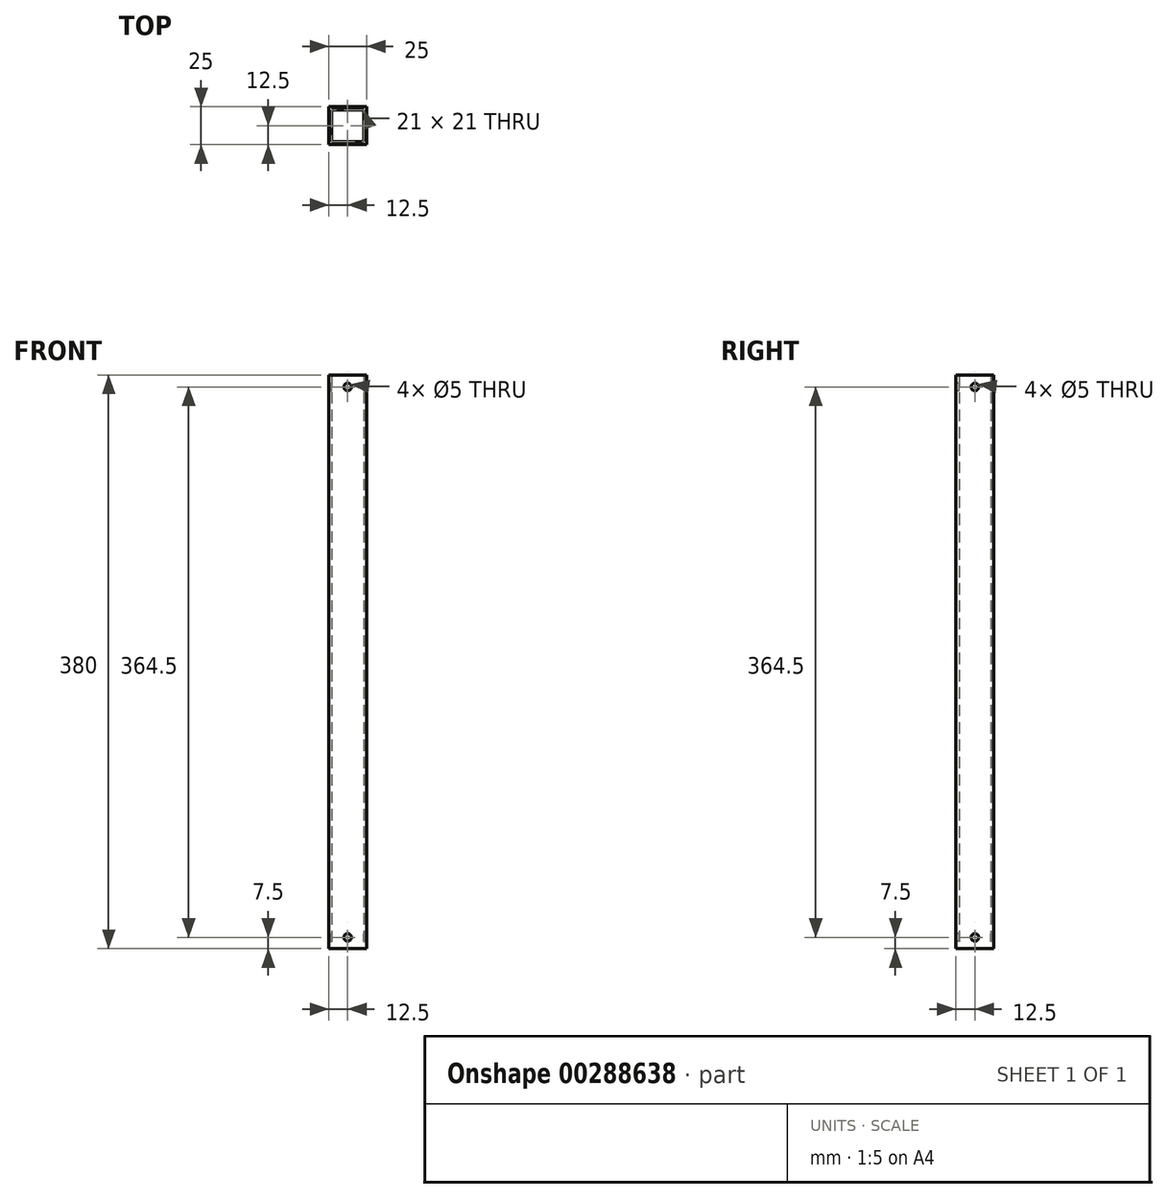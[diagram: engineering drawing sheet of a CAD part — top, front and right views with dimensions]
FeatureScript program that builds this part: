
annotation { "Feature Type Name" : "Feature", "Feature Type Description" : "" }
export const myFeature = defineFeature(function(context is Context, id is Id, definition is map)
    precondition{}
    {
        {
            var Q0;
            Q0=qCreatedBy(makeId("Top.planeOp"),FACE);
            var sketch = newSketch(context, id + "F0", { "sketchPlane" : qUnion([Q0])});
            skLineSegment(sketch, "E0.bottom", {"start": v(10.5, 10.5) * mm, "end": v(-10.5, 10.5) * mm});
            skLineSegment(sketch, "E0.top", {"start": v(10.5, -10.5) * mm, "end": v(-10.5, -10.5) * mm});
            skLineSegment(sketch, "E0.left", {"start": v(10.5, 10.5) * mm, "end": v(10.5, -10.5) * mm});
            skLineSegment(sketch, "E0.right", {"start": v(-10.5, 10.5) * mm, "end": v(-10.5, -10.5) * mm});
            skPoint(sketch, "E0.middle", {"position": v(0, 0) * mm});
            skLineSegment(sketch, "E1.bottom", {"start": v(12.5, 12.5) * mm, "end": v(-12.5, 12.5) * mm});
            skLineSegment(sketch, "E1.top", {"start": v(12.5, -12.5) * mm, "end": v(-12.5, -12.5) * mm});
            skLineSegment(sketch, "E1.left", {"start": v(12.5, 12.5) * mm, "end": v(12.5, -12.5) * mm});
            skLineSegment(sketch, "E1.right", {"start": v(-12.5, 12.5) * mm, "end": v(-12.5, -12.5) * mm});
            skSolve(sketch);
        }
        {
            var Q0;
            Q0=makeQuery(id+"F0.imprint","IMPRINT",FACE,{"disambiguationData":[TD([[makeQuery(id+"F0.imprint","IMPRINT",EDGE,{"derivedFrom":sQuery(id+"F0.wireOp",EDGE,"E0.bottom")}),-1.0]])]});
            extrude(context, id + "F1", {"entities" : qUnion([Q0]), "depth" : 380 * mm});
        }
        {
            var Q0;
            Q0=makeQuery(id+"F1.opExtrude","SWEPT_FACE",FACE,{"disambiguationData":[OSD([sQuery(id+"F0.wireOp",EDGE,"E1.top")])]});
            var sketch = newSketch(context, id + "F2", { "sketchPlane" : qUnion([Q0])});
            skCircle(sketch, "E2", {"center": v(0, 372) * mm, "radius": 2.5 * mm});
            skPoint(sketch, "E2.centerSnap0", {"position": v(0, 380) * mm});
            skCircle(sketch, "E3", {"center": v(0, 7.5) * mm, "radius": 2.5 * mm});
            skSolve(sketch);
        }
        {
            var Q0;
            Q0=makeQuery(id+"F2.imprint","IMPRINT",FACE,{"disambiguationData":[TD([[makeQuery(id+"F2.imprint","IMPRINT",EDGE,{"derivedFrom":sQuery(id+"F2.wireOp",EDGE,"E2")}),1.0]])]});
            var Q1;
            Q1=makeQuery(id+"F2.imprint","IMPRINT",FACE,{"disambiguationData":[TD([[makeQuery(id+"F2.imprint","IMPRINT",EDGE,{"derivedFrom":sQuery(id+"F2.wireOp",EDGE,"E3")}),1.0]])]});
            var Q2;
            Q2=sQuery(id+"F2.wireOp",EDGE,"E2");
            extrude(context, id + "F3", {"entities" : qUnion([Q0, Q1]), "operationType" : NewBodyOperationType.REMOVE, "surfaceEntities" : qUnion([Q2]), "oppositeDirection" : true, "depth" : 25 * mm, "offsetDistance" : 25 * mm});
        }
        {
            var Q0;
            Q0=makeQuery(id+"F1.opExtrude","SWEPT_FACE",FACE,{"disambiguationData":[OSD([sQuery(id+"F0.wireOp",EDGE,"E1.left")])]});
            var sketch = newSketch(context, id + "F4", { "sketchPlane" : qUnion([Q0])});
            skCircle(sketch, "E4", {"center": v(0, 7.5) * mm, "radius": 2.5 * mm});
            skPoint(sketch, "E4.centerSnap0", {"position": v(0, 0) * mm});
            skCircle(sketch, "E5", {"center": v(0, 372) * mm, "radius": 2.5 * mm});
            skPoint(sketch, "E5.centerSnap0", {"position": v(0, 380) * mm});
            skSolve(sketch);
        }
        {
            var Q0;
            Q0=makeQuery(id+"F4.imprint","IMPRINT",FACE,{"disambiguationData":[TD([[makeQuery(id+"F4.imprint","IMPRINT",EDGE,{"derivedFrom":sQuery(id+"F4.wireOp",EDGE,"E5")}),1.0]])]});
            var Q1;
            Q1=makeQuery(id+"F4.imprint","IMPRINT",FACE,{"disambiguationData":[TD([[makeQuery(id+"F4.imprint","IMPRINT",EDGE,{"derivedFrom":sQuery(id+"F4.wireOp",EDGE,"E4")}),1.0]])]});
            extrude(context, id + "F5", {"entities" : qUnion([Q0, Q1]), "operationType" : NewBodyOperationType.REMOVE, "oppositeDirection" : true, "depth" : 25 * mm, "offsetDistance" : 25 * mm});
        }
    });
